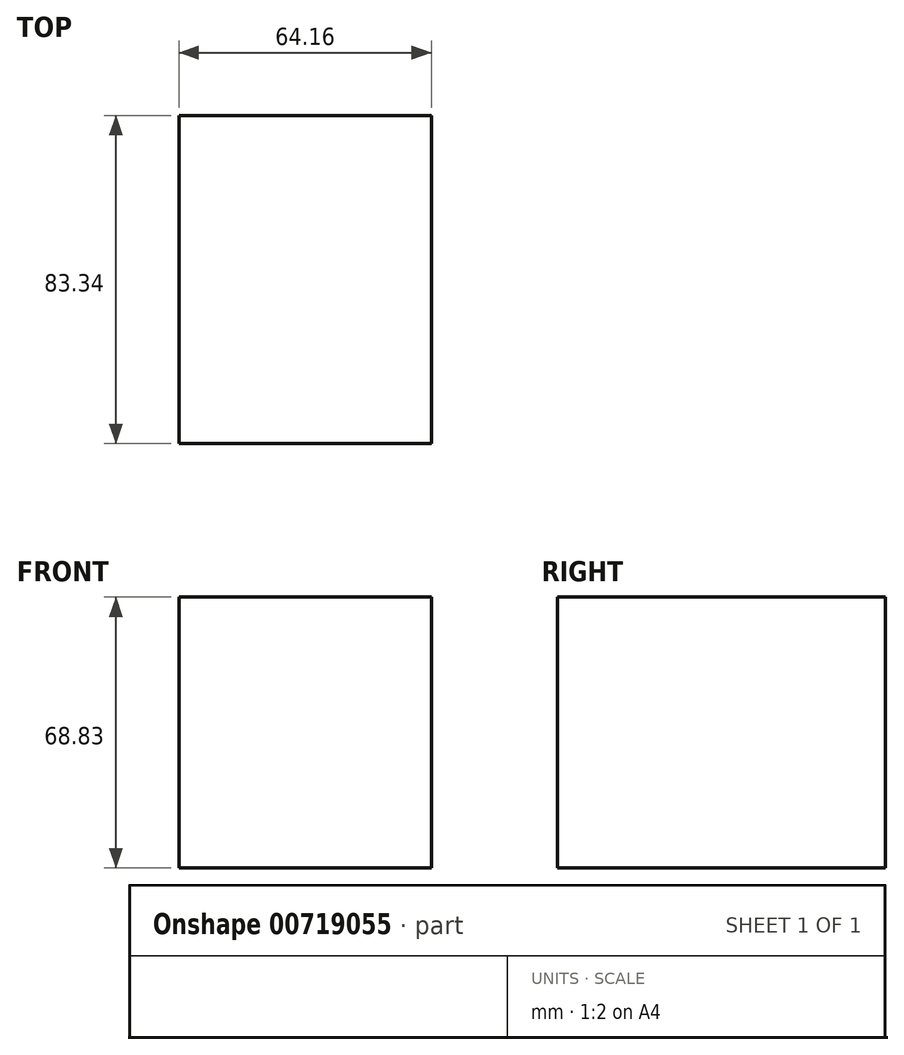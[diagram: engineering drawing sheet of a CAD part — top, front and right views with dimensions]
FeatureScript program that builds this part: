
annotation { "Feature Type Name" : "Feature", "Feature Type Description" : "" }
export const myFeature = defineFeature(function(context is Context, id is Id, definition is map)
    precondition{}
    {
        {
            var Q0;
            Q0=qCreatedBy(makeId("Top.planeOp"),FACE);
            var sketch = newSketch(context, id + "F0", { "sketchPlane" : qUnion([Q0])});
            skLineSegment(sketch, "E0.bottom", {"start": v(-32.08, -41.67) * mm, "end": v(32.08, -41.67) * mm});
            skLineSegment(sketch, "E0.top", {"start": v(-32.08, 41.67) * mm, "end": v(32.08, 41.67) * mm});
            skLineSegment(sketch, "E0.left", {"start": v(-32.08, -41.67) * mm, "end": v(-32.08, 41.67) * mm});
            skLineSegment(sketch, "E0.right", {"start": v(32.08, -41.67) * mm, "end": v(32.08, 41.67) * mm});
            skPoint(sketch, "E0.middle", {"position": v(0, 0) * mm});
            skSolve(sketch);
        }
        {
            var Q0;
            Q0 = qSketchRegion(id + "F0", true);
            extrude(context, id + "F1", {"entities" : qUnion([Q0]), "depth" : 68.83 * mm, "offsetDistance" : 25.4 * mm});
        }
    });
